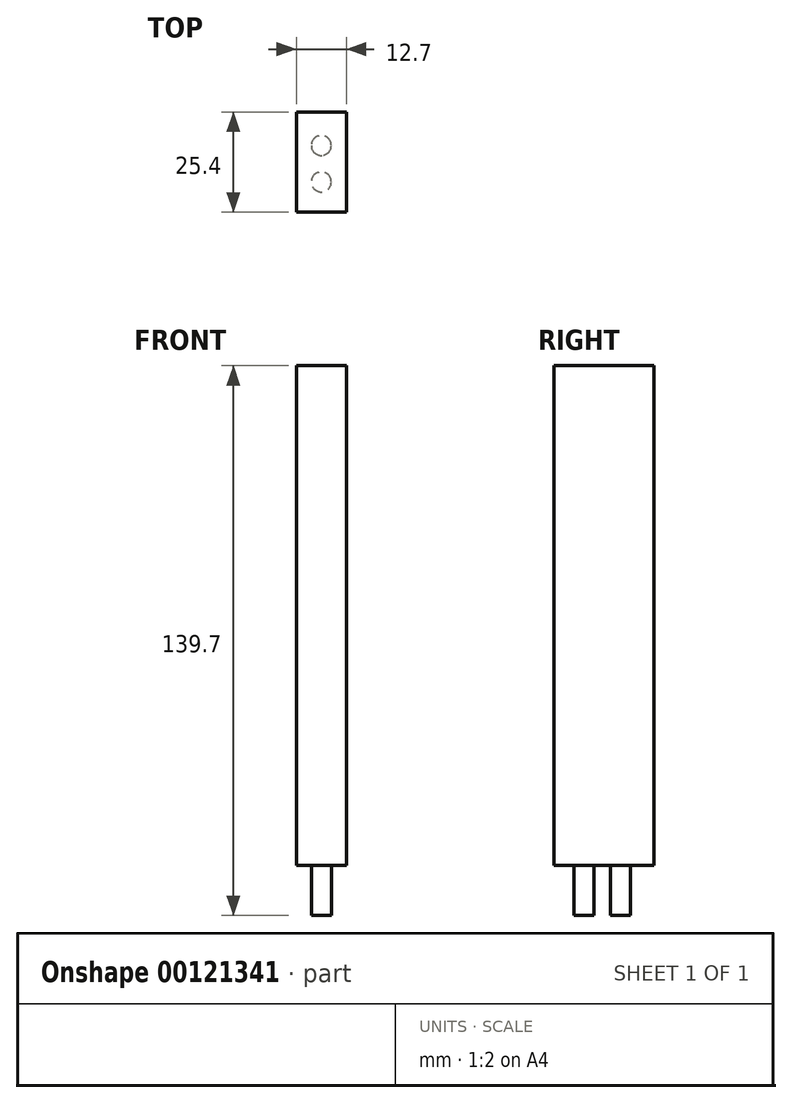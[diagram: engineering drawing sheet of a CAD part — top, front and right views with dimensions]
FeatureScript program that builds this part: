
annotation { "Feature Type Name" : "Feature", "Feature Type Description" : "" }
export const myFeature = defineFeature(function(context is Context, id is Id, definition is map)
    precondition{}
    {
        {
            var Q0;
            Q0=qCreatedBy(makeId("Top.planeOp"),FACE);
            var sketch = newSketch(context, id + "F0", { "sketchPlane" : qUnion([Q0])});
            skLineSegment(sketch, "E0.bottom", {"start": v(6.35, 12.7) * mm, "end": v(-6.35, 12.7) * mm});
            skLineSegment(sketch, "E0.top", {"start": v(6.35, -12.7) * mm, "end": v(-6.35, -12.7) * mm});
            skLineSegment(sketch, "E0.left", {"start": v(6.35, 12.7) * mm, "end": v(6.35, -12.7) * mm});
            skLineSegment(sketch, "E0.right", {"start": v(-6.35, 12.7) * mm, "end": v(-6.35, -12.7) * mm});
            skPoint(sketch, "E0.middle", {"position": v(0, 0) * mm});
            skSolve(sketch);
        }
        {
            var Q0;
            Q0 = qSketchRegion(id + "F0", true);
            extrude(context, id + "F1", {"entities" : qUnion([Q0]), "depth" : 127 * mm});
        }
        {
            var Q0;
            Q0=makeQuery(id+"F1.opExtrude","CAP_FACE",FACE,{"disambiguationData":[OSD([sQuery(id+"F0.wireOp",EDGE,"E0.bottom"),sQuery(id+"F0.wireOp",EDGE,"E0.top"),sQuery(id+"F0.wireOp",EDGE,"E0.left"),sQuery(id+"F0.wireOp",EDGE,"E0.right")])],"isStart":true});
            var sketch = newSketch(context, id + "F2", { "sketchPlane" : qUnion([Q0])});
            skCircle(sketch, "E1", {"center": v(0, 5.03) * mm, "radius": 2.54 * mm});
            skCircle(sketch, "E2", {"center": v(0, -4.22) * mm, "radius": 2.54 * mm});
            skPoint(sketch, "E2.centerSnap0", {"position": v(0, 12.7) * mm});
            skSolve(sketch);
        }
        {
            var Q0;
            Q0 = qSketchRegion(id + "F2", true);
            extrude(context, id + "F3", {"entities" : qUnion([Q0]), "operationType" : NewBodyOperationType.ADD, "depth" : 12.7 * mm});
        }
    });
